# Revit family: Hager-Golf-IP40-Plain_Door-syst-NoHosted-CH-de
name_source: partatom
category: Electrical Equipment
units: mm (PartAtom-declared; Revit-internal decimal feet)

## family parameters
Always vertical = Yes
Cut with Voids When Loaded = No
Panel Configuration = Two Columns, Circuits Across
Part Type = Panelboard
Room Calculation Point = No
Round Connector Dimension = Use Diameter
Shared = No
Work Plane-Based = Yes

## types (22) — shared parameters
Default Elevation = 1219 mm
EF000007 - Farbe = EV000202 - weiß
EF000116 - RAL-Nummer = 9010
EF000118 - Mit Montageplatte = No
EF000339 - Art der Abdeckung = EV004216 - Tür
EF001062 - EMV-Ausführung = No
EF001088 - Anbaumöglichkeit = Yes
EF001596 - Werkstoff des Gehäuses = EV000139 - Kunststoff
EF004462 - Art der Schließung = EV000154 - sonstige
EF006244 - Transparenter Deckel/Tür = No
EF006306 - Mit Schloss = No
EF009212 - Ausführung Deckel = EV000116 - geschlossen
EF015941 - Signaldurchlassende Tür = Yes
HG000001 - Anzahl der Spalten = 1
HG000002 - Mit tür = Yes
HG000003 - Bereich = Golf
HG000005 - Dicke = 3 mm  [stored 0.00984252 ft]
HG000009 - Doppelflügeligen Tür = No
HG000010 - Asymmetrische Türen = No
HG000011 - Leere Reihen von unten = No
HG000017 - Distanz zwischen den Polen = 18 mm  [stored 0.0590551 ft]
Manufacturer = Hager
Type Comments = Golf
zero-valued in all types: HG000007 - Anzahl der leeren Spalten, HG000008 - Anzahl der leeren Reihen

## per-type parameters (varying)
| type | EF000003 - Montageart | EF000008 - Breite | EF000040 - Höhe | EF000049 - Tiefe | EF000218 - Einbautiefe | EF000266 - Anzahl der Reihen | EF000332 - Einbauhöhe | EF000846 - Einbaubreite | EF001131 - Innentiefe | EF001134 - DIN-Schiene | EF002950 - Breite in Teilungseinheiten | EF005474 - Schutzart (IP) | EF015776 - Erdungsklemmenblock | EF015777 - Neutralleiterklemmenblock | HG000004 - Herstellerreferenz | HG000006 - Unterputz | Model |
| Aufputz  B138 H184 T99 4 Teilungseinheiten - VS104PS | EV000384 - Aufputz | 138 mm  [stored 0.452756 ft] | 184 mm  [stored 0.603675 ft] | 99 mm  [stored 0.324803 ft] | 0 mm  [stored 0 ft] | 1 | 0 mm  [stored 0 ft] | 0 mm  [stored 0 ft] | 99 mm  [stored 0.324803 ft] | Yes | 4 |  | No | No | VS104PS | No | VS104PS |
| Aufputz  B210 H184 T99 8 Teilungseinheiten - VS108PS | EV000384 - Aufputz | 210 mm  [stored 0.688976 ft] | 184 mm  [stored 0.603675 ft] | 99 mm  [stored 0.324803 ft] | 0 mm  [stored 0 ft] | 1 | 0 mm  [stored 0 ft] | 0 mm  [stored 0 ft] | 99 mm  [stored 0.324803 ft] | No | 8 |  | No | No | VS108PS | No | VS108PS |
| Aufputz IP40 B282 H252 T99 12 Teilungseinheiten - VS112PS | EV000384 - Aufputz | 282 mm | 252 mm  [stored 0.826772 ft] | 99 mm  [stored 0.324803 ft] | 0 mm  [stored 0 ft] | 1 | 0 mm  [stored 0 ft] | 0 mm  [stored 0 ft] | 99 mm  [stored 0.324803 ft] | Yes | 12 | EV006415 - IP40 | Yes | Yes | VS112PS | No | VS112PS |
| Aufputz IP40 B282 H377 T99 12 Teilungseinheiten - VS212PS | EV000384 - Aufputz | 282 mm | 377 mm  [stored 1.23688 ft] | 99 mm  [stored 0.324803 ft] | 0 mm  [stored 0 ft] | 2 | 0 mm  [stored 0 ft] | 0 mm  [stored 0 ft] | 99 mm  [stored 0.324803 ft] | Yes | 12 | EV006415 - IP40 | Yes | Yes | VS212PS | No | VS212PS |
| Aufputz IP40 B282 H500 T99 12 Teilungseinheiten - VS312PS | EV000384 - Aufputz | 282 mm | 500 mm  [stored 1.64042 ft] | 99 mm  [stored 0.324803 ft] | 0 mm  [stored 0 ft] | 3 | 0 mm  [stored 0 ft] | 0 mm  [stored 0 ft] | 99 mm  [stored 0.324803 ft] | Yes | 12 | EV006415 - IP40 | Yes | Yes | VS312PS | No | VS312PS |
| Aufputz IP40 B282 H647 T99 12 Teilungseinheiten - VS412PS | EV000384 - Aufputz | 282 mm | 647 mm  [stored 2.1227 ft] | 99 mm  [stored 0.324803 ft] | 0 mm  [stored 0 ft] | 4 | 0 mm  [stored 0 ft] | 0 mm  [stored 0 ft] | 99 mm  [stored 0.324803 ft] | Yes | 12 | EV006415 - IP40 | Yes | Yes | VS412PS | No | VS412PS |
| Aufputz IP40 B390 H252 T99 18 Teilungseinheiten - VS118PS | EV000384 - Aufputz | 390 mm  [stored 1.27953 ft] | 252 mm  [stored 0.826772 ft] | 99 mm  [stored 0.324803 ft] | 0 mm  [stored 0 ft] | 1 | 0 mm  [stored 0 ft] | 0 mm  [stored 0 ft] | 99 mm  [stored 0.324803 ft] | Yes | 18 | EV006415 - IP40 | Yes | Yes | VS118PS | No | VS118PS |
| Aufputz IP40 B390 H377 T99 18 Teilungseinheiten - VS218PS | EV000384 - Aufputz | 390 mm  [stored 1.27953 ft] | 377 mm  [stored 1.23688 ft] | 99 mm  [stored 0.324803 ft] | 0 mm  [stored 0 ft] | 2 | 0 mm  [stored 0 ft] | 0 mm  [stored 0 ft] | 99 mm  [stored 0.324803 ft] | Yes | 18 | EV006415 - IP40 | Yes | Yes | VS218PS | No | VS218PS |
| Aufputz IP40 B390 H500 T99 18 Teilungseinheiten - VS318PS | EV000384 - Aufputz | 390 mm  [stored 1.27953 ft] | 500 mm  [stored 1.64042 ft] | 99 mm  [stored 0.324803 ft] | 0 mm  [stored 0 ft] | 3 | 0 mm  [stored 0 ft] | 0 mm  [stored 0 ft] | 99 mm  [stored 0.324803 ft] | Yes | 18 | EV006415 - IP40 | Yes | Yes | VS318PS | No | VS318PS |
| Aufputz IP40 B390 H647 T99 18 Teilungseinheiten - VS418PS | EV000384 - Aufputz | 390 mm  [stored 1.27953 ft] | 647 mm  [stored 2.1227 ft] | 99 mm  [stored 0.324803 ft] | 0 mm  [stored 0 ft] | 4 | 0 mm  [stored 0 ft] | 0 mm  [stored 0 ft] | 99 mm  [stored 0.324803 ft] | Yes | 18 | EV006415 - IP40 | Yes | Yes | VS418PS | No | VS418PS |
| Aufputz IP40 B462 H252 T99 22 Teilungseinheiten - VS122PS | EV000384 - Aufputz | 462 mm  [stored 1.51575 ft] | 252 mm  [stored 0.826772 ft] | 99 mm  [stored 0.324803 ft] | 0 mm  [stored 0 ft] | 1 | 0 mm  [stored 0 ft] | 0 mm  [stored 0 ft] | 99 mm  [stored 0.324803 ft] | Yes | 22 | EV006415 - IP40 | Yes | Yes | VS122PS | No | VS122PS |
| Unterputz  B204 H225 T97.5 4 Teilungseinheiten - VF104PS | EV000383 - Unterputz | 204 mm | 225 mm  [stored 0.738189 ft] | 98 mm  [stored 0.321522 ft] | 72 mm  [stored 0.23622 ft] | 1 | 189 mm  [stored 0.620079 ft] | 170 mm  [stored 0.557743 ft] | 98 mm  [stored 0.321522 ft] | Yes | 4 |  | No | No | VF104PS | Yes | VF104PS |
| Unterputz  B275 H225 T97.5 8 Teilungseinheiten - VF108PS | EV000383 - Unterputz | 275 mm | 225 mm  [stored 0.738189 ft] | 98 mm  [stored 0.321522 ft] | 72 mm  [stored 0.23622 ft] | 1 | 189 mm  [stored 0.620079 ft] | 242 mm  [stored 0.793963 ft] | 98 mm  [stored 0.321522 ft] | Yes | 8 |  | No | No | VF108PS | Yes | VF108PS |
| Unterputz IP40 B352 H293 T97.5 12 Teilungseinheiten - VF112PS | EV000383 - Unterputz | 352 mm  [stored 1.15486 ft] | 293 mm | 98 mm  [stored 0.321522 ft] | 72 mm  [stored 0.23622 ft] | 1 | 257 mm  [stored 0.843176 ft] | 318 mm  [stored 1.04331 ft] | 98 mm  [stored 0.321522 ft] | Yes | 12 | EV006415 - IP40 | Yes | Yes | VF112PS | Yes | VF112PS |
| Unterputz IP40 B352 H543 T97.5 12 Teilungseinheiten - VF312PS | EV000383 - Unterputz | 352 mm  [stored 1.15486 ft] | 543 mm  [stored 1.7815 ft] | 98 mm  [stored 0.321522 ft] | 72 mm  [stored 0.23622 ft] | 3 | 507 mm  [stored 1.66339 ft] | 318 mm  [stored 1.04331 ft] | 98 mm  [stored 0.321522 ft] | Yes | 12 | EV006415 - IP40 | Yes | Yes | VF312PS | Yes | VF312PS |
| Unterputz IP40 B352 H688 T97.5 12 Teilungseinheiten - VF412PS | EV000383 - Unterputz | 352 mm  [stored 1.15486 ft] | 688 mm  [stored 2.25722 ft] | 98 mm  [stored 0.321522 ft] | 72 mm  [stored 0.23622 ft] | 4 | 652 mm  [stored 2.13911 ft] | 318 mm  [stored 1.04331 ft] | 98 mm  [stored 0.321522 ft] | Yes | 12 | EV006415 - IP40 | Yes | Yes | VF412PS | Yes | VF412PS |
| Unterputz IP40 B382 H418 T97.5 12 Teilungseinheiten - VF212PS | EV000383 - Unterputz | 382 mm  [stored 1.25328 ft] | 418 mm  [stored 1.37139 ft] | 98 mm  [stored 0.321522 ft] | 72 mm  [stored 0.23622 ft] | 2 | 382 mm  [stored 1.25328 ft] | 318 mm  [stored 1.04331 ft] | 98 mm  [stored 0.321522 ft] | Yes | 12 | EV006415 - IP40 | Yes | Yes | VF212PS | Yes | VF212PS |
| Unterputz IP40 B460 H293 T97.5 18 Teilungseinheiten - VF118PS | EV000383 - Unterputz | 460 mm  [stored 1.50919 ft] | 293 mm | 98 mm  [stored 0.321522 ft] | 72 mm  [stored 0.23622 ft] | 1 | 257 mm  [stored 0.843176 ft] | 426 mm  [stored 1.39764 ft] | 98 mm  [stored 0.321522 ft] | Yes | 18 | EV006415 - IP40 | Yes | Yes | VF118PS | Yes | VF118PS |
| Unterputz IP40 B460 H418 T97.5 18 Teilungseinheiten - VF218PS | EV000383 - Unterputz | 460 mm  [stored 1.50919 ft] | 418 mm  [stored 1.37139 ft] | 98 mm  [stored 0.321522 ft] | 72 mm  [stored 0.23622 ft] | 2 | 382 mm  [stored 1.25328 ft] | 426 mm  [stored 1.39764 ft] | 98 mm  [stored 0.321522 ft] | Yes | 18 | EV006415 - IP40 | Yes | Yes | VF218PS | Yes | VF218PS |
| Unterputz IP40 B460 H543 T97.5 18 Teilungseinheiten - VF318PS | EV000383 - Unterputz | 460 mm  [stored 1.50919 ft] | 543 mm  [stored 1.7815 ft] | 98 mm  [stored 0.321522 ft] | 72 mm  [stored 0.23622 ft] | 3 | 507 mm  [stored 1.66339 ft] | 426 mm  [stored 1.39764 ft] | 98 mm  [stored 0.321522 ft] | Yes | 18 | EV006415 - IP40 | Yes | Yes | VF318PS | Yes | VF318PS |
| Unterputz IP40 B460 H688 T97.5 18 Teilungseinheiten - VF418PS | EV000383 - Unterputz | 460 mm  [stored 1.50919 ft] | 688 mm  [stored 2.25722 ft] | 98 mm  [stored 0.321522 ft] | 72 mm  [stored 0.23622 ft] | 4 | 652 mm  [stored 2.13911 ft] | 426 mm  [stored 1.39764 ft] | 98 mm  [stored 0.321522 ft] | Yes | 18 | EV006415 - IP40 | Yes | Yes | VF418PS | Yes | VF418PS |
| Unterputz IP40 B532 H293 T97.5 22 Teilungseinheiten - VF122PS | EV000383 - Unterputz | 532 mm  [stored 1.74541 ft] | 293 mm | 98 mm  [stored 0.321522 ft] | 72 mm  [stored 0.23622 ft] | 1 | 257 mm  [stored 0.843176 ft] | 498 mm  [stored 1.63386 ft] | 98 mm  [stored 0.321522 ft] | Yes | 22 | EV006415 - IP40 | Yes | Yes | VF122PS | Yes | VF122PS |

note: [stored X ft] marks values corroborated as IEEE doubles in the binary element streams (Revit-internal decimal feet)

## geometry (parser evidence)
native form markers: Sweep x13
no freeform markers — native parametric forms only
